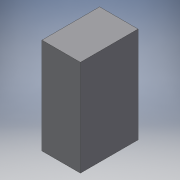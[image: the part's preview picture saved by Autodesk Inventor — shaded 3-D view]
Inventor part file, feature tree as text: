
AUTODESK INVENTOR PART (.ipt)
format: ipt  version: 2019 (Build 230136000, 136)  size: 116,736 bytes
history: native  units: in
note: dims shown in document units (in); Inventor stores cm internally (conversion verified against a paired STEP export)
features: extrude x3, sketch x3, fillet x1
ambient origin geometry x8: Origin, YZ Plane, XZ Plane, XY Plane, X Axis, Y Axis, Z Axis, Center Point
bodies: Solid1 (feature_tree)
feature tree (7):
  extrude  "Extrusion1"  Depth=1.9685in
  fillet  "Fillet1"  Radius=0.7874in
  extrude  "Extrusion2"  Depth=0.125in
  extrude  "Extrusion3"  Depth=1.1811in
  sketch  "Sketch1"  dims[d0=1.1811in d1=1.9685in d2=0.7874in d3=0.0in]
  sketch  "Sketch2"  dims[d4=0.125in d5=0.1299in]
  sketch  "Sketch3"  dims[d6=0.1969in d7=0.1299in d8=0.1969in d9=1.1811in d10=0.0in d11=0.315in d12=1.1811in d13=0.0in]
